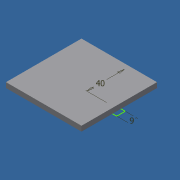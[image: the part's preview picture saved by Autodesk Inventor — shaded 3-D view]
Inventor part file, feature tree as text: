
AUTODESK INVENTOR PART (.ipt)
format: ipt  version: 2018 (Build 220112000, 112)  size: 82,432 bytes
history: native  units: mm
features: sketch x2, other x1, extrude x1
ambient origin geometry x8: Origin, YZ Plane, XZ Plane, XY Plane, X Axis, Y Axis, Z Axis, Center Point
bodies: Solid1 (feature_tree)
feature tree (4):
  other  "<userpath>\OneDrive\Objet3D\3DPrinter\Parameters.xlsx"
  extrude  "Extrusion1"  Depth=80.0mm
  sketch  "Sketch2"  dims[d2=5.4mm d3=0.0mm d4=40.0mm d6=9.0mm]
  sketch  "Sketch1"  dims[d0=80.0mm d1=80.0mm]
